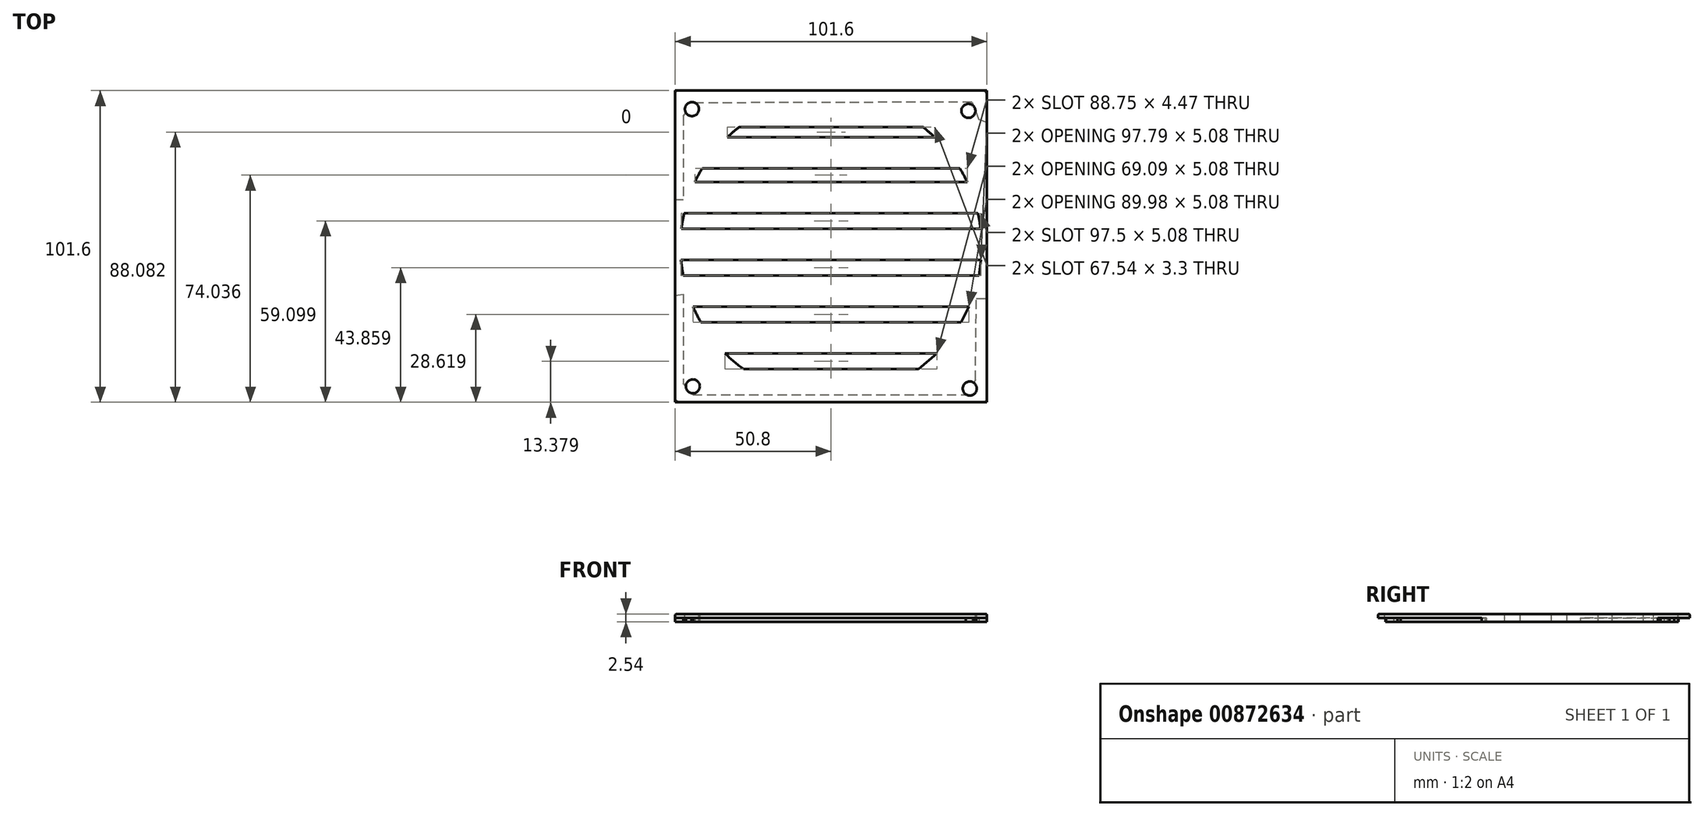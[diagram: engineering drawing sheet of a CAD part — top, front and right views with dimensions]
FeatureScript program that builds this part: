
annotation { "Feature Type Name" : "Feature", "Feature Type Description" : "" }
export const myFeature = defineFeature(function(context is Context, id is Id, definition is map)
    precondition{}
    {
        {
            var Q0;
            Q0=qCreatedBy(makeId("Top.planeOp"),FACE);
            var sketch = newSketch(context, id + "F0", { "sketchPlane" : qUnion([Q0])});
            skLineSegment(sketch, "E0.bottom", {"start": v(-50.8, -50.8) * mm, "end": v(50.8, -50.8) * mm});
            skLineSegment(sketch, "E0.top", {"start": v(-50.8, 50.8) * mm, "end": v(50.8, 50.8) * mm});
            skLineSegment(sketch, "E0.left", {"start": v(-50.8, -50.8) * mm, "end": v(-50.8, 50.8) * mm});
            skLineSegment(sketch, "E0.right", {"start": v(50.8, -50.8) * mm, "end": v(50.8, 50.8) * mm});
            skPoint(sketch, "E0.middle", {"position": v(0, 0) * mm});
            skCircle(sketch, "E1", {"center": v(0, 0) * mm, "radius": 50.28 * mm});
            skSolve(sketch);
        }
        {
            var Q0;
            Q0 = qSketchRegion(id + "F0", true);
            var Q1;
            Q1=makeQuery(id+"F0.imprint","IMPRINT",FACE,{"disambiguationData":[TD([[makeQuery(id+"F0.imprint","IMPRINT",EDGE,{"derivedFrom":sQuery(id+"F0.wireOp",EDGE,"E1")}),1.0]])]});
            extrude(context, id + "F1", {"entities" : qUnion([Q0, Q1]), "depth" : 2.54 * mm, "offsetDistance" : 25.4 * mm});
        }
        {
            var Q0;
            Q0=makeQuery(id+"F1.opExtrude","CAP_FACE",FACE,{"disambiguationData":[OSD([sQuery(id+"F0.wireOp",EDGE,"E0.bottom"),sQuery(id+"F0.wireOp",EDGE,"E0.top"),sQuery(id+"F0.wireOp",EDGE,"E0.left"),sQuery(id+"F0.wireOp",EDGE,"E0.right")])],"isStart":false});
            var sketch = newSketch(context, id + "F2", { "sketchPlane" : qUnion([Q0])});
            skCircle(sketch, "E2", {"center": v(0, 0) * mm, "radius": 49.1 * mm});
            skLineSegment(sketch, "E3", {"start": v(-29.9, 38.93) * mm, "end": v(29.9, 38.93) * mm});
            skLineSegment(sketch, "E4", {"start": v(-33.77, 35.63) * mm, "end": v(33.77, 35.63) * mm});
            skLineSegment(sketch, "E5", {"start": v(-41.97, 25.47) * mm, "end": v(41.97, 25.47) * mm});
            skLineSegment(sketch, "E6", {"start": v(-44.37, 21) * mm, "end": v(44.37, 21) * mm});
            skLineSegment(sketch, "E7", {"start": v(-47.88, 10.84) * mm, "end": v(47.88, 10.84) * mm});
            skLineSegment(sketch, "E8", {"start": v(-48.9, -4.4) * mm, "end": v(48.9, -4.4) * mm});
            skLineSegment(sketch, "E9", {"start": v(48.9, -4.4) * mm, "end": v(48.17, -9.48) * mm});
            skLineSegment(sketch, "E10", {"start": v(48.17, -9.48) * mm, "end": v(-48.17, -9.48) * mm});
            skLineSegment(sketch, "E11", {"start": v(-48.17, -9.48) * mm, "end": v(-45, -19.64) * mm});
            skLineSegment(sketch, "E12", {"start": v(-45, -19.64) * mm, "end": v(45, -19.64) * mm});
            skLineSegment(sketch, "E13", {"start": v(45, -19.64) * mm, "end": v(42.41, -24.72) * mm});
            skLineSegment(sketch, "E14", {"start": v(42.41, -24.72) * mm, "end": v(-42.41, -24.72) * mm});
            skLineSegment(sketch, "E15", {"start": v(-42.41, -24.72) * mm, "end": v(-34.54, -34.88) * mm});
            skLineSegment(sketch, "E16", {"start": v(-34.54, -34.88) * mm, "end": v(34.54, -34.88) * mm});
            skLineSegment(sketch, "E17", {"start": v(34.54, -34.88) * mm, "end": v(28.51, -39.96) * mm});
            skLineSegment(sketch, "E18", {"start": v(28.51, -39.96) * mm, "end": v(-28.51, -39.96) * mm});
            skLineSegment(sketch, "E19", {"start": v(-48.75, 5.76) * mm, "end": v(48.75, 5.76) * mm});
            skPoint(sketch, "E20", {"position": v(0, 49.1) * mm});
            skPoint(sketch, "E20.positionSnap0", {"position": v(0, 50.8) * mm});
            skPoint(sketch, "E21", {"position": v(0, 38.93) * mm});
            skPoint(sketch, "E22", {"position": v(0, 35.63) * mm});
            skPoint(sketch, "E23", {"position": v(0, 25.47) * mm});
            skPoint(sketch, "E24", {"position": v(0, 21) * mm});
            skPoint(sketch, "E25", {"position": v(0, 10.84) * mm});
            skPoint(sketch, "E26", {"position": v(0, 5.76) * mm});
            skPoint(sketch, "E27", {"position": v(0, -4.4) * mm});
            skPoint(sketch, "E28", {"position": v(0, -9.48) * mm});
            skPoint(sketch, "E29", {"position": v(0, -19.64) * mm});
            skPoint(sketch, "E30", {"position": v(0.72, -27.92) * mm});
            skPoint(sketch, "E31", {"position": v(0, -34.88) * mm});
            skPoint(sketch, "E32", {"position": v(0.24, -40.26) * mm});
            skPoint(sketch, "E33", {"position": v(0, -24.72) * mm});
            skSolve(sketch);
        }
        {
            var Q0;
            {var subQ0=sQuery(id+"F2.wireOp",EDGE,"E3");Q0=makeQuery(id+"F2.imprint","IMPRINT",FACE,{"disambiguationData":[TD([[makeQuery(id+"F2.imprint","IMPRINT",EDGE,{"derivedFrom":subQ0}),-1.0]])]});}
            var Q1;
            {var subQ0=sQuery(id+"F2.wireOp",EDGE,"E5");Q1=makeQuery(id+"F2.imprint","IMPRINT",FACE,{"disambiguationData":[TD([[makeQuery(id+"F2.imprint","IMPRINT",EDGE,{"derivedFrom":subQ0}),-1.0]])]});}
            var Q2;
            {var subQ0=sQuery(id+"F2.wireOp",EDGE,"E7");Q2=makeQuery(id+"F2.imprint","IMPRINT",FACE,{"disambiguationData":[TD([[makeQuery(id+"F2.imprint","IMPRINT",EDGE,{"derivedFrom":subQ0}),-1.0]])]});}
            var Q3;
            {var subQ0=sQuery(id+"F2.wireOp",EDGE,"E8");Q3=makeQuery(id+"F2.imprint","IMPRINT",FACE,{"disambiguationData":[TD([[makeQuery(id+"F2.imprint","IMPRINT",EDGE,{"derivedFrom":subQ0}),-1.0]])]});}
            var Q4;
            {var subQ0=sQuery(id+"F2.wireOp",EDGE,"E12");Q4=makeQuery(id+"F2.imprint","IMPRINT",FACE,{"disambiguationData":[TD([[makeQuery(id+"F2.imprint","IMPRINT",EDGE,{"derivedFrom":subQ0}),-1.0]])]});}
            var Q5;
            {var subQ0=sQuery(id+"F2.wireOp",EDGE,"E16");Q5=makeQuery(id+"F2.imprint","IMPRINT",FACE,{"disambiguationData":[TD([[makeQuery(id+"F2.imprint","IMPRINT",EDGE,{"derivedFrom":subQ0}),-1.0]])]});}
            extrude(context, id + "F3", {"entities" : qUnion([Q0, Q1, Q2, Q3, Q4, Q5]), "operationType" : NewBodyOperationType.REMOVE, "endBound" : BoundingType.THROUGH_ALL, "oppositeDirection" : true, "depth" : 2.54 * mm, "offsetDistance" : 25.4 * mm});
        }
        {
            var Q0;
            Q0=makeQuery(id+"F1.opExtrude","CAP_FACE",FACE,{"disambiguationData":[OSD([sQuery(id+"F0.wireOp",EDGE,"E0.bottom"),sQuery(id+"F0.wireOp",EDGE,"E0.top"),sQuery(id+"F0.wireOp",EDGE,"E0.left"),sQuery(id+"F0.wireOp",EDGE,"E0.right")])],"isStart":true});
            var sketch = newSketch(context, id + "F4", { "sketchPlane" : qUnion([Q0])});
            skPoint(sketch, "E34", {"position": v(-45.04, 48.35) * mm});
            skPoint(sketch, "E35", {"position": v(-48.2, 44.6) * mm});
            skPoint(sketch, "E36", {"position": v(-48.2, 15.54) * mm});
            skPoint(sketch, "E37", {"position": v(-50.8, 15.97) * mm});
            skPoint(sketch, "E38", {"position": v(43.9, 48.35) * mm});
            skPoint(sketch, "E39", {"position": v(47.06, 43.46) * mm});
            skPoint(sketch, "E40", {"position": v(47.35, 16.98) * mm});
            skPoint(sketch, "E41", {"position": v(45.9, -47.06) * mm});
            skPoint(sketch, "E42", {"position": v(-45, -46.77) * mm});
            skPoint(sketch, "E43", {"position": v(-48.17, -42.45) * mm});
            skPoint(sketch, "E44", {"position": v(48.17, -41.3) * mm});
            skLineSegment(sketch, "E45", {"start": v(-45.04, 48.35) * mm, "end": v(43.9, 48.35) * mm});
            skLineSegment(sketch, "E46", {"start": v(47.06, 43.46) * mm, "end": v(43.9, 48.35) * mm});
            skLineSegment(sketch, "E47", {"start": v(47.06, 43.46) * mm, "end": v(47.35, 16.98) * mm});
            skLineSegment(sketch, "E48", {"start": v(50.8, 16.98) * mm, "end": v(50.8, -40.44) * mm});
            skLineSegment(sketch, "E49", {"start": v(45.9, -47.06) * mm, "end": v(48.17, -41.3) * mm});
            skLineSegment(sketch, "E50", {"start": v(50.8, -40.44) * mm, "end": v(48.17, -41.3) * mm});
            skLineSegment(sketch, "E51", {"start": v(45.9, -47.06) * mm, "end": v(-45, -46.77) * mm});
            skLineSegment(sketch, "E52", {"start": v(-48.17, -42.45) * mm, "end": v(-48.17, -15.1) * mm});
            skLineSegment(sketch, "E53", {"start": v(-48.17, -15.1) * mm, "end": v(-50.8, -15.1) * mm});
            skLineSegment(sketch, "E54", {"start": v(-50.8, -15.1) * mm, "end": v(-50.8, 15.97) * mm});
            skLineSegment(sketch, "E55", {"start": v(-48.2, 15.54) * mm, "end": v(-48.2, 44.6) * mm});
            skLineSegment(sketch, "E56", {"start": v(-45.04, 48.35) * mm, "end": v(-48.2, 44.6) * mm});
            skLineSegment(sketch, "E57", {"start": v(47.35, 16.98) * mm, "end": v(50.8, 16.98) * mm});
            skLineSegment(sketch, "E58", {"start": v(-50.8, 15.97) * mm, "end": v(-48.2, 15.54) * mm});
            skLineSegment(sketch, "E59", {"start": v(-48.17, -42.45) * mm, "end": v(-45, -46.77) * mm});
            skSolve(sketch);
        }
        {
            var Q0;
            Q0=makeQuery(id+"F4.imprint","IMPRINT",FACE,{"disambiguationData":[TD([[makeQuery(id+"F4.imprint","IMPRINT",EDGE,{"derivedFrom":sQuery(id+"F4.wireOp",EDGE,"E45")}),1.0]])]});
            var Q1;
            Q1=makeQuery(id+"F4.imprint","IMPRINT",FACE,{"disambiguationData":[TD([[makeQuery(id+"F4.imprint","IMPRINT",EDGE,{"derivedFrom":sQuery(id+"F4.wireOp",EDGE,"E49")}),-1.0]])]});
            extrude(context, id + "F5", {"entities" : qUnion([Q0, Q1]), "operationType" : NewBodyOperationType.REMOVE, "oppositeDirection" : true, "depth" : 1.27 * mm, "offsetDistance" : 25.4 * mm});
        }
        {
            var Q0;
            Q0=makeQuery(id+"F1.opExtrude","CAP_EDGE",EDGE,{"disambiguationData":[OSD([sQuery(id+"F0.wireOp",EDGE,"E0.top")])],"isStart":false});
            var Q1;
            Q1=makeQuery(id+"F1.opExtrude","CAP_EDGE",EDGE,{"disambiguationData":[OSD([sQuery(id+"F0.wireOp",EDGE,"E0.left")])],"isStart":false});
            var Q2;
            Q2=makeQuery(id+"F1.opExtrude","CAP_EDGE",EDGE,{"disambiguationData":[OSD([sQuery(id+"F0.wireOp",EDGE,"E0.bottom")])],"isStart":false});
            var Q3;
            Q3=makeQuery(id+"F1.opExtrude","CAP_EDGE",EDGE,{"disambiguationData":[OSD([sQuery(id+"F0.wireOp",EDGE,"E0.right")])],"isStart":false});
            fillet(context, id + "F6", {"entities" : qUnion([Q0, Q1, Q2, Q3]), "tangentPropagation" : true, "radius" : 0.5 * mm, "defaultsChanged" : false, "vertexSettings" : [], "allowEdgeOverflow" : false});
        }
        {
            var Q0;
            Q0=makeQuery(id+"F1.opExtrude","CAP_FACE",FACE,{"disambiguationData":[OSD([sQuery(id+"F0.wireOp",EDGE,"E0.bottom"),sQuery(id+"F0.wireOp",EDGE,"E0.top"),sQuery(id+"F0.wireOp",EDGE,"E0.left"),sQuery(id+"F0.wireOp",EDGE,"E0.right")])],"isStart":false});
            var sketch = newSketch(context, id + "F7", { "sketchPlane" : qUnion([Q0])});
            skPoint(sketch, "E60", {"position": v(-45.33, 44.75) * mm});
            skPoint(sketch, "E61", {"position": v(44.75, 44.18) * mm});
            skPoint(sketch, "E62", {"position": v(45.2, -46.34) * mm});
            skPoint(sketch, "E63", {"position": v(-44.47, -46.2) * mm});
            skCircle(sketch, "E64", {"center": v(-45.33, 44.75) * mm, "radius": 2.29 * mm});
            skCircle(sketch, "E65", {"center": v(44.75, 44.18) * mm, "radius": 2.29 * mm});
            skCircle(sketch, "E66", {"center": v(45.2, -46.34) * mm, "radius": 2.29 * mm});
            skCircle(sketch, "E67", {"center": v(-44.47, -46.2) * mm, "radius": 2.29 * mm});
            skSolve(sketch);
        }
        {
            var Q0;
            Q0=makeQuery(id+"F7.imprint","IMPRINT",FACE,{"disambiguationData":[TD([[makeQuery(id+"F7.imprint","IMPRINT",EDGE,{"derivedFrom":sQuery(id+"F7.wireOp",EDGE,"E64")}),1.0]])]});
            var Q1;
            Q1=makeQuery(id+"F7.imprint","IMPRINT",FACE,{"disambiguationData":[TD([[makeQuery(id+"F7.imprint","IMPRINT",EDGE,{"derivedFrom":sQuery(id+"F7.wireOp",EDGE,"E65")}),1.0]])]});
            var Q2;
            Q2=makeQuery(id+"F7.imprint","IMPRINT",FACE,{"disambiguationData":[TD([[makeQuery(id+"F7.imprint","IMPRINT",EDGE,{"derivedFrom":sQuery(id+"F7.wireOp",EDGE,"E66")}),1.0]])]});
            extrude(context, id + "F8", {"entities" : qUnion([Q0, Q1, Q2]), "operationType" : NewBodyOperationType.REMOVE, "endBound" : BoundingType.THROUGH_ALL, "oppositeDirection" : true, "depth" : 25.4 * mm, "offsetDistance" : 25.4 * mm});
        }
        {
            var Q0;
            Q0=makeQuery(id+"F1.opExtrude","CAP_FACE",FACE,{"disambiguationData":[OSD([sQuery(id+"F0.wireOp",EDGE,"E0.bottom"),sQuery(id+"F0.wireOp",EDGE,"E0.top"),sQuery(id+"F0.wireOp",EDGE,"E0.left"),sQuery(id+"F0.wireOp",EDGE,"E0.right")])],"isStart":false});
            var sketch = newSketch(context, id + "F9", { "sketchPlane" : qUnion([Q0])});
            skPoint(sketch, "E68", {"position": v(-45.04, -45.62) * mm});
            skCircle(sketch, "E69", {"center": v(-45.04, -45.62) * mm, "radius": 2.29 * mm});
            skSolve(sketch);
        }
        {
            var Q0;
            Q0=makeQuery(id+"F9.imprint","IMPRINT",FACE,{"disambiguationData":[TD([[makeQuery(id+"F9.imprint","IMPRINT",EDGE,{"derivedFrom":sQuery(id+"F9.wireOp",EDGE,"E69")}),1.0]])]});
            extrude(context, id + "F10", {"entities" : qUnion([Q0]), "operationType" : NewBodyOperationType.REMOVE, "endBound" : BoundingType.THROUGH_ALL, "oppositeDirection" : true, "depth" : 25.4 * mm, "offsetDistance" : 25.4 * mm});
        }
    });
